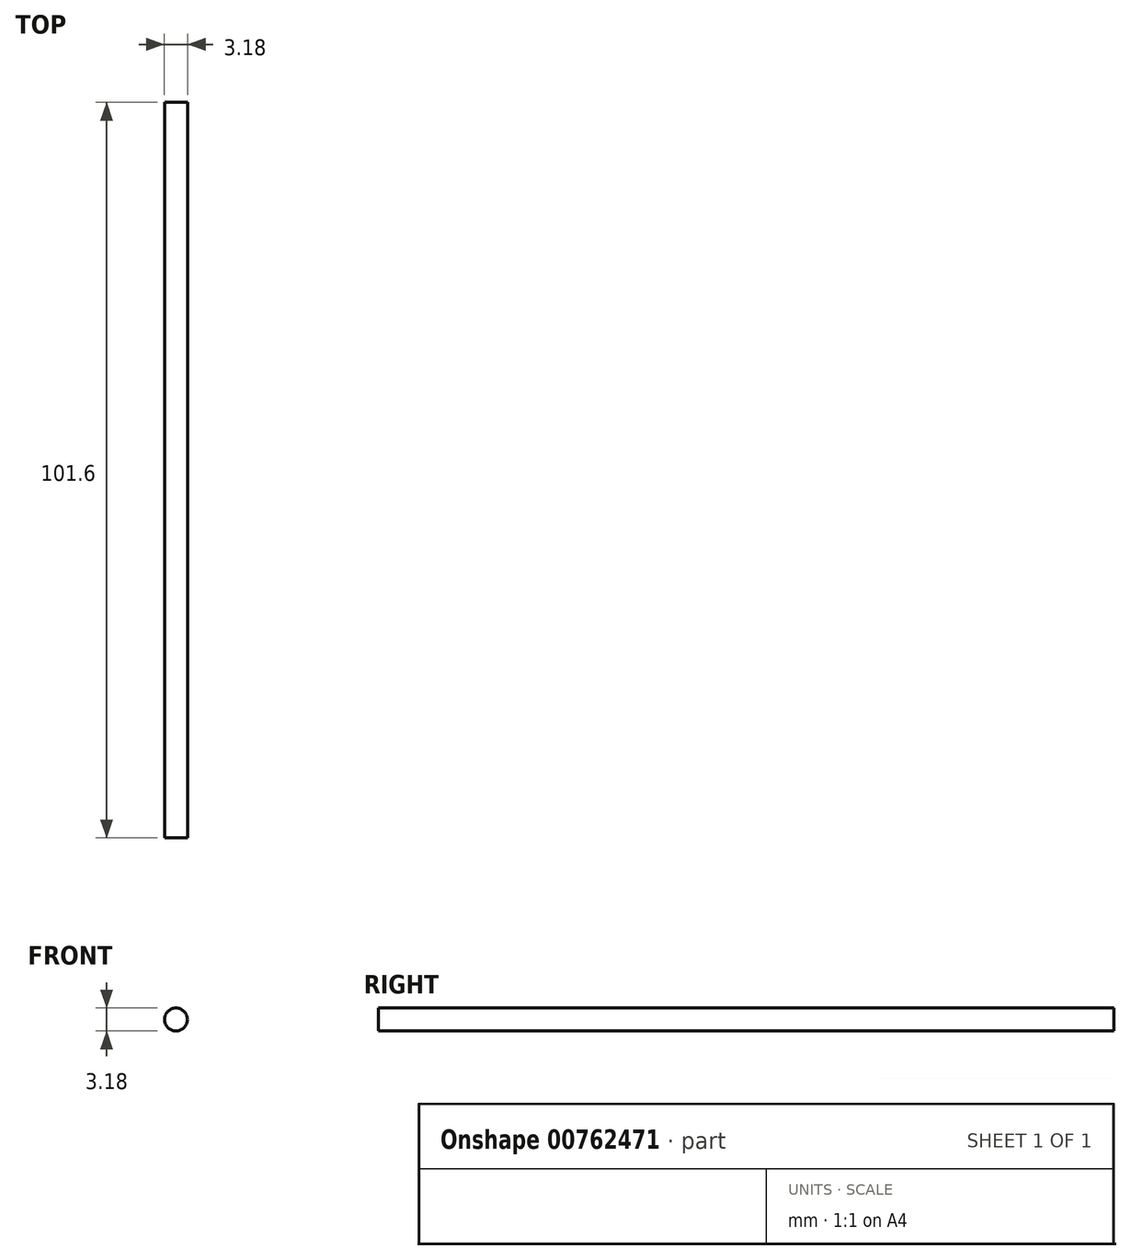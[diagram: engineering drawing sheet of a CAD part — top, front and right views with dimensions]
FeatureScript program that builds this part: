
annotation { "Feature Type Name" : "Feature", "Feature Type Description" : "" }
export const myFeature = defineFeature(function(context is Context, id is Id, definition is map)
    precondition{}
    {
        {
            var Q0;
            Q0=qCreatedBy(makeId("Front.planeOp"),FACE);
            var sketch = newSketch(context, id + "F0", { "sketchPlane" : qUnion([Q0])});
            skCircle(sketch, "E0", {"center": v(0, 0) * mm, "radius": 1.59 * mm});
            skSolve(sketch);
        }
        {
            var Q0;
            Q0 = qSketchRegion(id + "F0", true);
            extrude(context, id + "F1", {"entities" : qUnion([Q0]), "depth" : 101.6 * mm, "offsetDistance" : 25.4 * mm});
        }
    });
